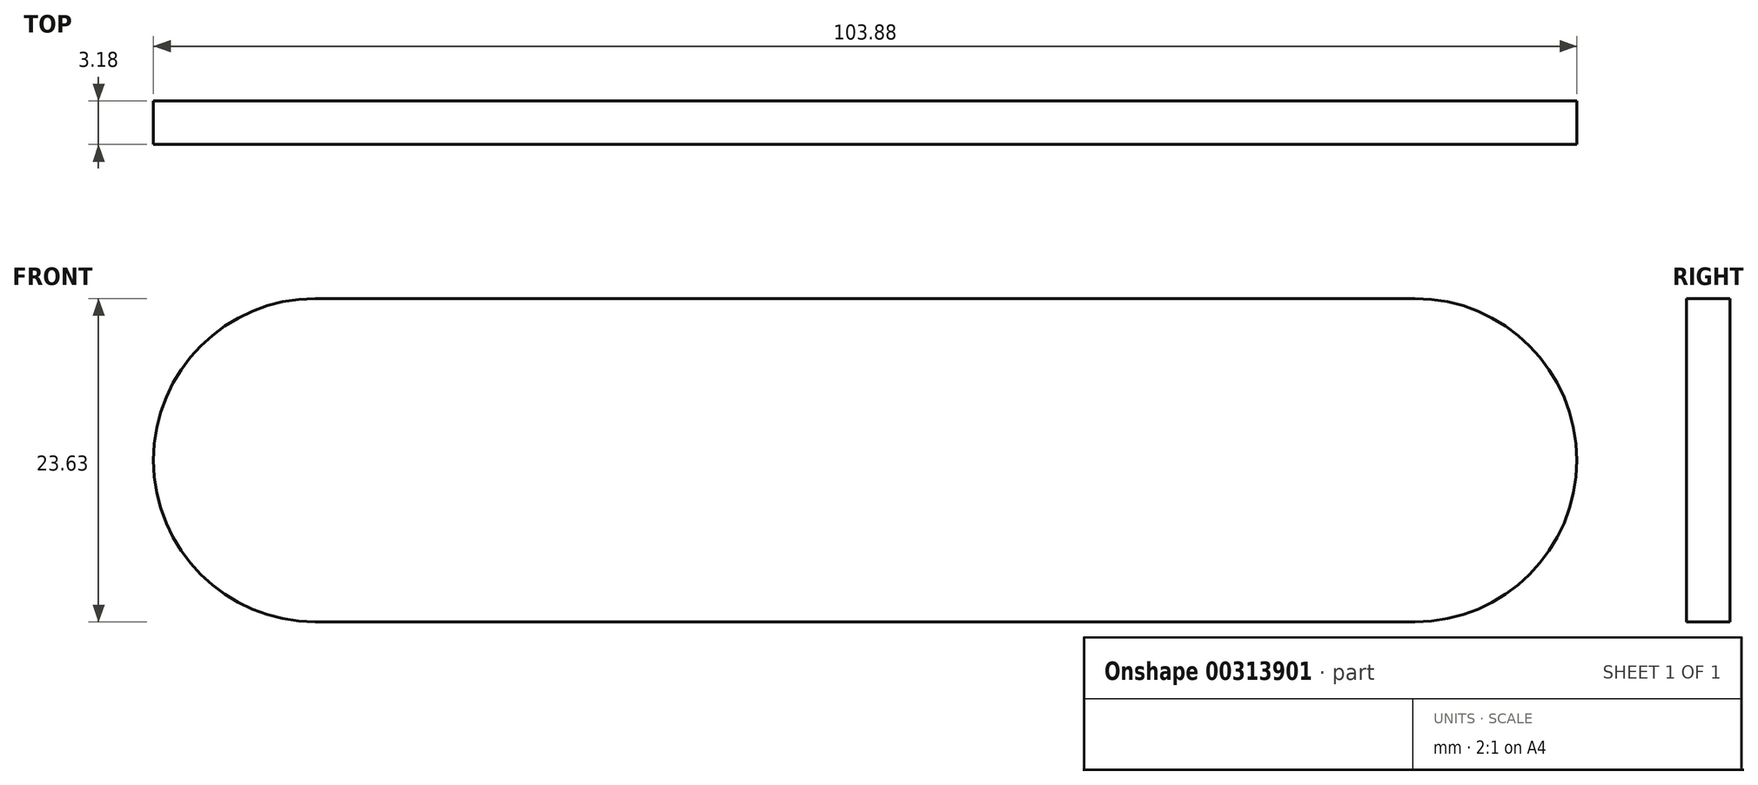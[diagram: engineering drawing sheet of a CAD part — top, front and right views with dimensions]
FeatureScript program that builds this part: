
annotation { "Feature Type Name" : "Feature", "Feature Type Description" : "" }
export const myFeature = defineFeature(function(context is Context, id is Id, definition is map)
    precondition{}
    {
        {
            var Q0;
            Q0=qCreatedBy(makeId("Front.planeOp"),FACE);
            var sketch = newSketch(context, id + "F0", { "sketchPlane" : qUnion([Q0])});
            skLineSegment(sketch, "E0", {"start": v(-41.02, 23.63) * mm, "end": v(39.23, 23.63) * mm});
            skLineSegment(sketch, "E1", {"start": v(-41.02, 0) * mm, "end": v(39.23, 0) * mm});
            skArc(sketch, "E2", {"start": v(-41.02, 23.63) * mm, "mid": v(-52.83, 11.81) * mm, "end": v(-41.02, 0) * mm});
            skArc(sketch, "E3", {"start": v(39.23, 0) * mm, "mid": v(51.05, 11.81) * mm, "end": v(39.23, 23.63) * mm});
            skSolve(sketch);
        }
        {
            var Q0;
            Q0=makeQuery(id+"F0.imprint","IMPRINT",FACE,{"disambiguationData":[TD([[makeQuery(id+"F0.imprint","IMPRINT",EDGE,{"derivedFrom":sQuery(id+"F0.wireOp",EDGE,"E0")}),-1.0]])]});
            extrude(context, id + "F1", {"entities" : qUnion([Q0]), "endBound" : BoundingType.SYMMETRIC, "depth" : 3.17 * mm});
        }
        {
            var Q0;
            Q0=makeQuery(id+"F1.opExtrude","SWEPT_BODY",BODY,{"disambiguationData":[OSD([sQuery(id+"F0.wireOp",EDGE,"E0"),sQuery(id+"F0.wireOp",EDGE,"E1"),sQuery(id+"F0.wireOp",EDGE,"E2"),sQuery(id+"F0.wireOp",EDGE,"E3")])]});
            transform(context, id + "F2", {"entities" : qUnion([Q0]), "transformType" : TransformType.TRANSLATION_3D, "dx" : 0 * mm, "dy" : 0 * mm, "dz" : 0 * mm, "makeCopy" : true});
        }
        {
            var Q0;
            Q0=makeQuery(id+"F2.opPattern","COPY",BODY,{"derivedFrom":makeQuery(id+"F1.opExtrude","SWEPT_BODY",BODY,{"disambiguationData":[OSD([sQuery(id+"F0.wireOp",EDGE,"E0"),sQuery(id+"F0.wireOp",EDGE,"E1"),sQuery(id+"F0.wireOp",EDGE,"E2"),sQuery(id+"F0.wireOp",EDGE,"E3")])]}),"instanceName":"1"});
            transform(context, id + "F3", {"entities" : qUnion([Q0]), "transformType" : TransformType.TRANSLATION_3D, "dx" : 0 * mm, "dy" : 0 * mm, "dz" : 0 * mm, "makeCopy" : true});
        }
    });
